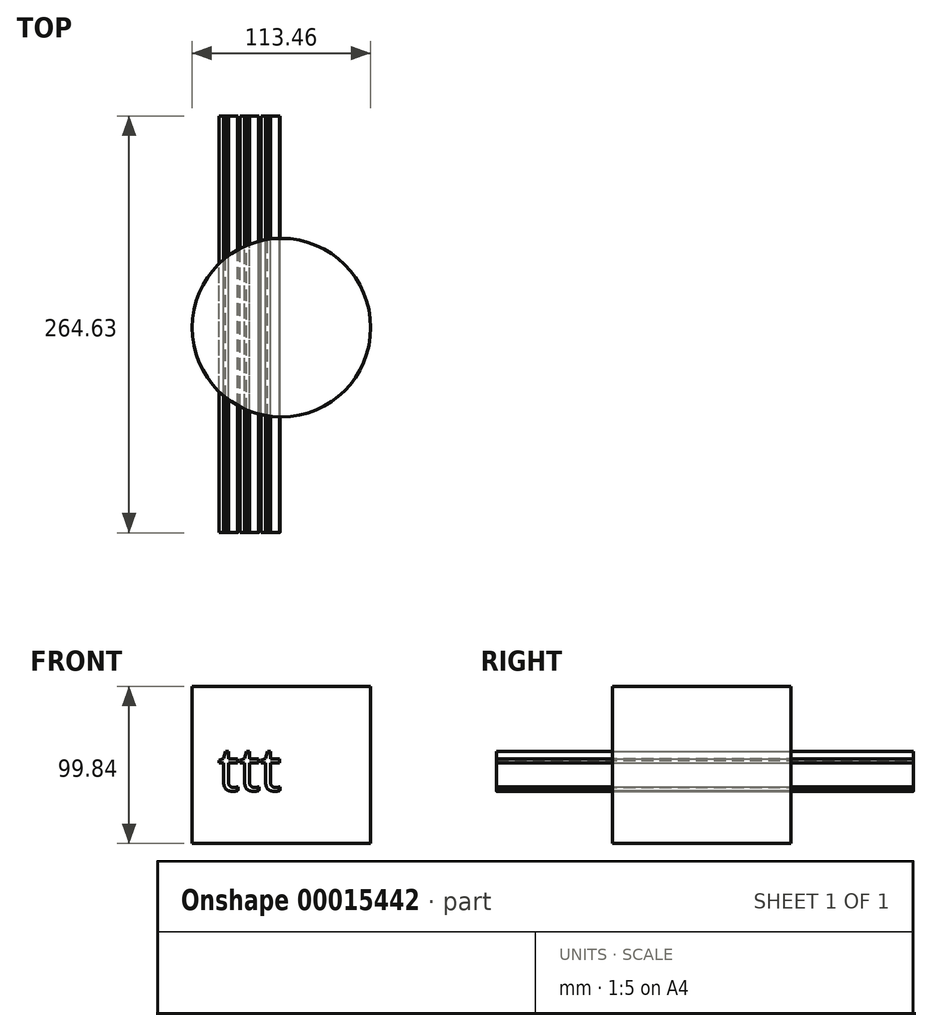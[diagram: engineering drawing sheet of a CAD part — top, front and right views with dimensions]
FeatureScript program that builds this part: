
annotation { "Feature Type Name" : "Feature", "Feature Type Description" : "" }
export const myFeature = defineFeature(function(context is Context, id is Id, definition is map)
    precondition{}
    {
        {
            var Q0;
            Q0=qCreatedBy(makeId("Top.planeOp"),FACE);
            var sketch = newSketch(context, id + "F0", { "sketchPlane" : qUnion([Q0])});
            skCircle(sketch, "E0", {"center": v(0, 0) * mm, "radius": 56.73 * mm});
            skSolve(sketch);
        }
        {
            var Q0;
            Q0=qCreatedBy(makeId("Front.planeOp"),FACE);
            var sketch = newSketch(context, id + "F1", { "sketchPlane" : qUnion([Q0])});
            skText(sketch, "E1", { "text": "ttt", "fontName": "OpenSans-Regular.ttf"});
            const initialGuessF1  = {"E1": [-0.04022, 0.03338, 1, 0, 0.0272]};
            skSetInitialGuess(sketch, initialGuessF1);
            skSolve(sketch);
        }
        {
            var Q0;
            Q0=makeQuery(id+"F1.imprint","IMPRINT",FACE,{"disambiguationData":[TD([[makeQuery(id+"F1.imprint","IMPRINT",EDGE,{"derivedFrom":sQuery(id+"F1.wireOp",EDGE,"E1.sketch_text.stroke-0")}),-1.0]])]});
            var Q1;
            Q1=makeQuery(id+"F1.imprint","IMPRINT",FACE,{"disambiguationData":[TD([[makeQuery(id+"F1.imprint","IMPRINT",EDGE,{"derivedFrom":sQuery(id+"F1.wireOp",EDGE,"E1.sketch_text.stroke-19")}),-1.0]])]});
            var Q2;
            Q2=makeQuery(id+"F1.imprint","IMPRINT",FACE,{"disambiguationData":[TD([[makeQuery(id+"F1.imprint","IMPRINT",EDGE,{"derivedFrom":sQuery(id+"F1.wireOp",EDGE,"E1.sketch_text.stroke-38")}),-1.0]])]});
            extrude(context, id + "F2", {"entities" : qUnion([Q0, Q1, Q2]), "depth" : 130.27 * mm, "hasSecondDirection" : true, "secondDirectionOppositeDirection" : true, "secondDirectionDepth" : 134.36 * mm});
        }
        {
            var Q0;
            Q0=makeQuery(id+"F0.imprint","IMPRINT",FACE,{"disambiguationData":[TD([[makeQuery(id+"F0.imprint","IMPRINT",EDGE,{"derivedFrom":sQuery(id+"F0.wireOp",EDGE,"E0")}),1.0]])]});
            extrude(context, id + "F3", {"entities" : qUnion([Q0]), "depth" : 99.84 * mm});
        }
    });
